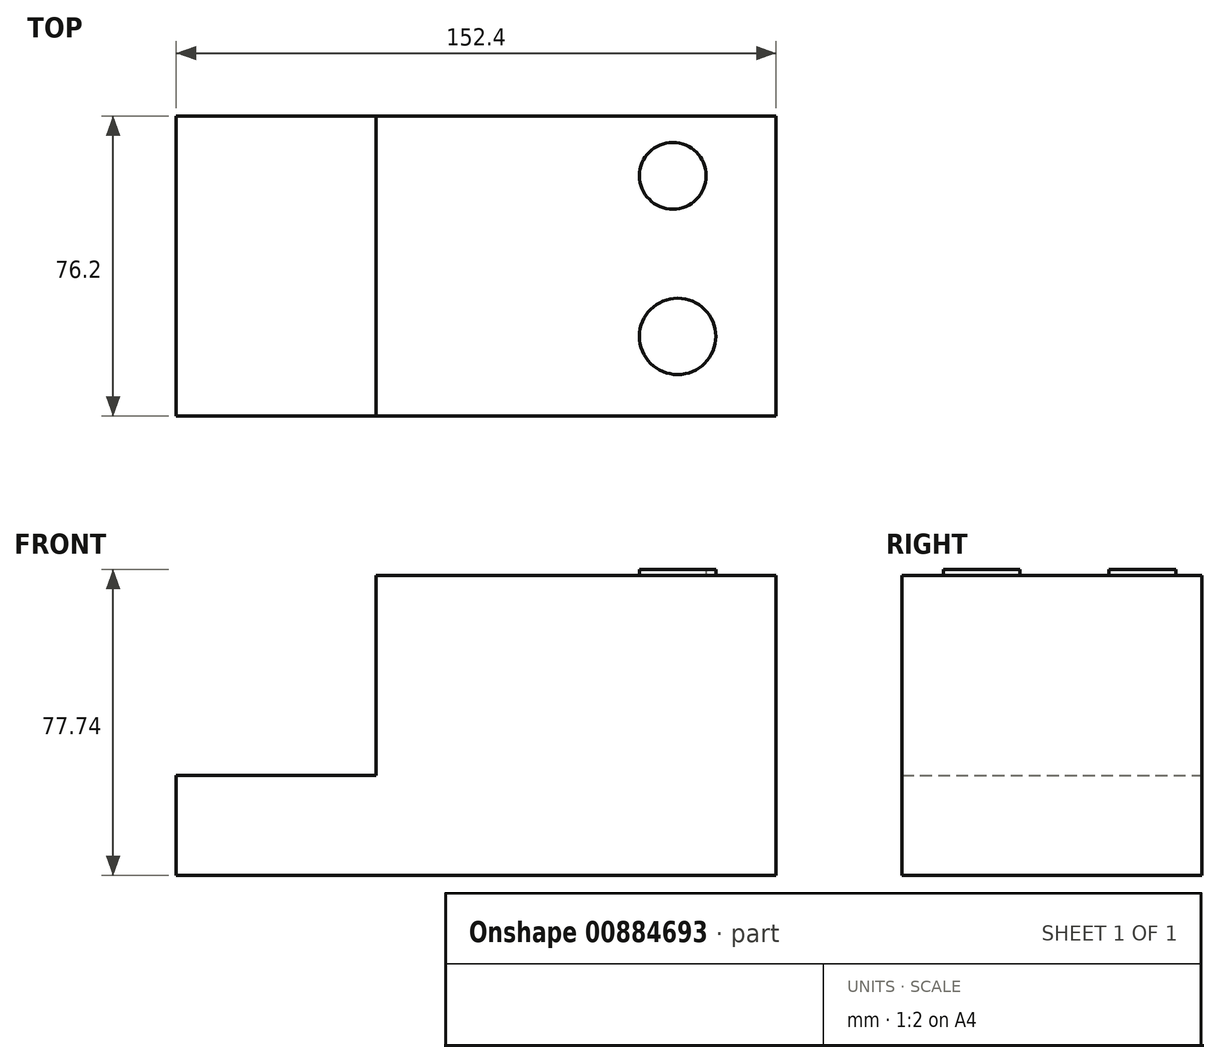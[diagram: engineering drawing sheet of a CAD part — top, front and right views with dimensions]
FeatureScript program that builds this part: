
annotation { "Feature Type Name" : "Feature", "Feature Type Description" : "" }
export const myFeature = defineFeature(function(context is Context, id is Id, definition is map)
    precondition{}
    {
        {
            var Q0;
            Q0=qCreatedBy(makeId("Front.planeOp"),FACE);
            var sketch = newSketch(context, id + "F0", { "sketchPlane" : qUnion([Q0])});
            skLineSegment(sketch, "E0.bottom", {"start": v(-96.98, -6.37) * mm, "end": v(-46.18, -6.37) * mm});
            skLineSegment(sketch, "E0.top", {"start": v(-96.98, 19.03) * mm, "end": v(-46.18, 19.03) * mm});
            skLineSegment(sketch, "E0.left", {"start": v(-96.98, -6.37) * mm, "end": v(-96.98, 19.03) * mm});
            skLineSegment(sketch, "E0.right", {"start": v(-46.18, -6.37) * mm, "end": v(-46.18, 19.03) * mm});
            skLineSegment(sketch, "E1.bottom", {"start": v(-46.18, -6.37) * mm, "end": v(55.42, -6.37) * mm});
            skLineSegment(sketch, "E1.top", {"start": v(-46.18, 69.83) * mm, "end": v(55.42, 69.83) * mm});
            skLineSegment(sketch, "E1.left", {"start": v(-46.18, -6.37) * mm, "end": v(-46.18, 69.83) * mm});
            skLineSegment(sketch, "E1.right", {"start": v(55.42, -6.37) * mm, "end": v(55.42, 69.83) * mm});
            skSolve(sketch);
        }
        {
            var Q0;
            Q0 = qSketchRegion(id + "F0", true);
            extrude(context, id + "F1", {"entities" : qUnion([Q0]), "depth" : 76.2 * mm, "offsetDistance" : 25.4 * mm});
        }
        {
            var Q0;
            Q0=qCreatedBy(makeId("Top.planeOp"),FACE);
            var sketch = newSketch(context, id + "F2", { "sketchPlane" : qUnion([Q0])});
            skCircle(sketch, "E2", {"center": v(29.2, -15.15) * mm, "radius": 8.47 * mm});
            skCircle(sketch, "E3", {"center": v(30.4, -55.98) * mm, "radius": 9.7 * mm});
            skSolve(sketch);
        }
        {
            var Q0;
            Q0 = qSketchRegion(id + "F2", true);
            extrude(context, id + "F3", {"entities" : qUnion([Q0]), "operationType" : NewBodyOperationType.ADD, "depth" : 71.37 * mm, "offsetDistance" : 25.4 * mm});
        }
    });
